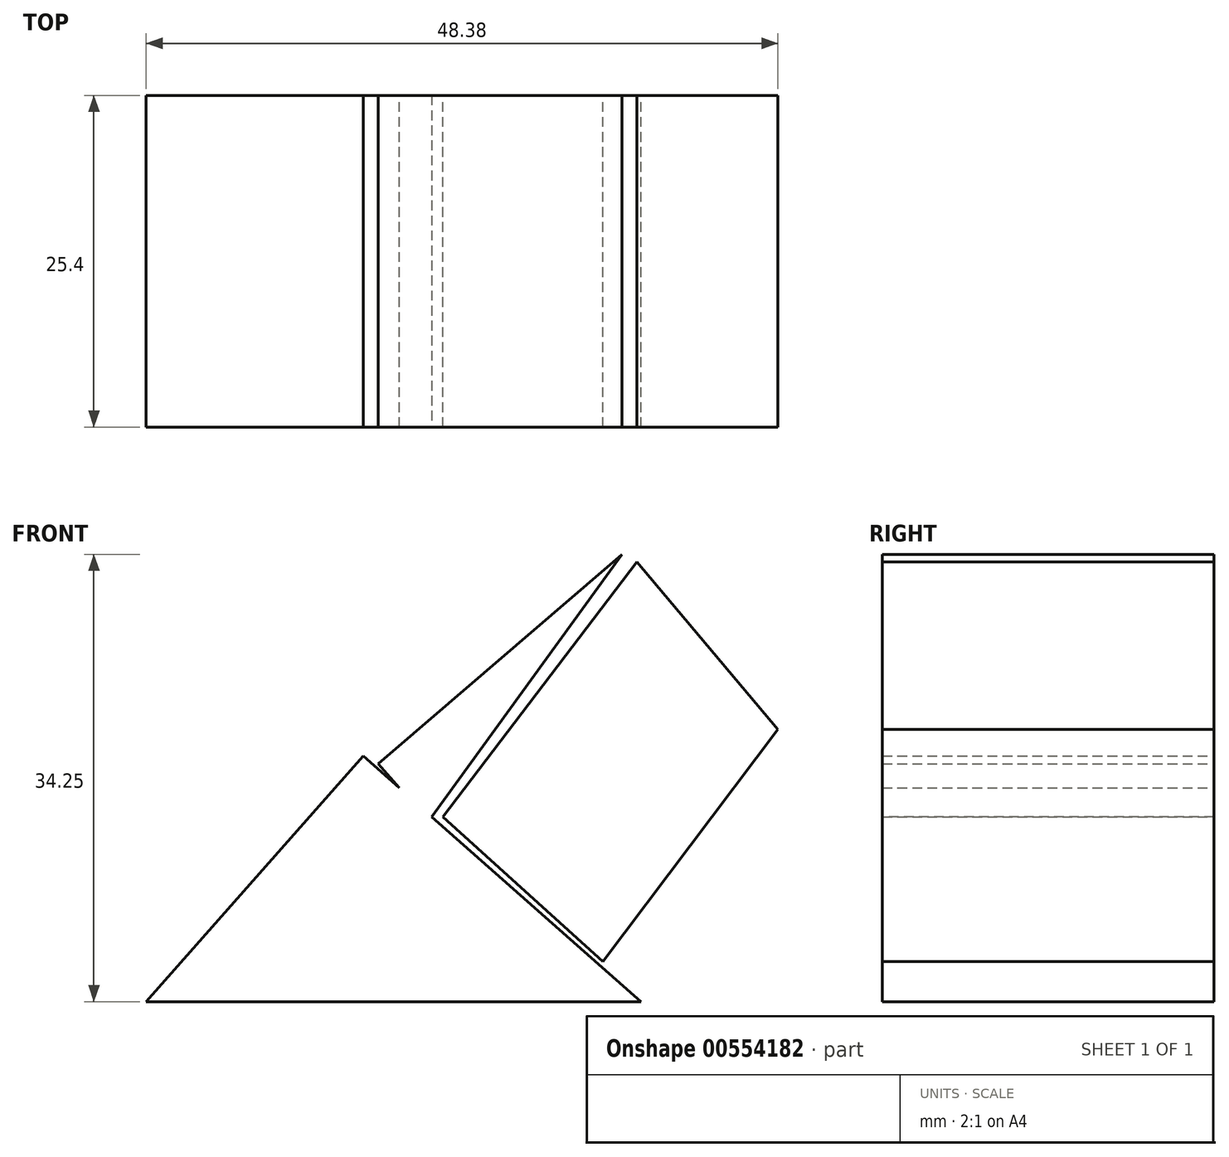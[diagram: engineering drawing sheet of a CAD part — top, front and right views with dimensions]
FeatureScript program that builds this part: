
annotation { "Feature Type Name" : "Feature", "Feature Type Description" : "" }
export const myFeature = defineFeature(function(context is Context, id is Id, definition is map)
    precondition{}
    {
        {
            var Q0;
            Q0=qCreatedBy(makeId("Front.planeOp"),FACE);
            var sketch = newSketch(context, id + "F0", { "sketchPlane" : qUnion([Q0])});
            skLineSegment(sketch, "E0", {"start": v(-48.38, 0) * mm, "end": v(-31.77, 18.8) * mm});
            skLineSegment(sketch, "E1", {"start": v(-31.77, 18.8) * mm, "end": v(-10.5, 0) * mm});
            skLineSegment(sketch, "E2", {"start": v(-10.5, 0) * mm, "end": v(-48.38, 0) * mm});
            skSolve(sketch);
        }
        {
            var Q0;
            Q0 = qSketchRegion(id + "F0", true);
            extrude(context, id + "F1", {"entities" : qUnion([Q0]), "depth" : 25.4 * mm, "offsetDistance" : 25.4 * mm});
        }
        {
            var Q0;
            Q0=qCreatedBy(makeId("Front.planeOp"),FACE);
            var sketch = newSketch(context, id + "F2", { "sketchPlane" : qUnion([Q0])});
            skLineSegment(sketch, "E3", {"start": v(-25.65, 14.14) * mm, "end": v(-10.78, 33.67) * mm});
            skLineSegment(sketch, "E4", {"start": v(-10.78, 33.67) * mm, "end": v(0, 20.84) * mm});
            skLineSegment(sketch, "E5", {"start": v(0, 20.84) * mm, "end": v(-13.4, 3.06) * mm});
            skLineSegment(sketch, "E6", {"start": v(-13.4, 3.06) * mm, "end": v(-25.65, 14.14) * mm});
            skSolve(sketch);
        }
        {
            var Q0;
            Q0 = qSketchRegion(id + "F2", true);
            extrude(context, id + "F3", {"entities" : qUnion([Q0]), "depth" : 25.4 * mm, "offsetDistance" : 25.4 * mm});
        }
        {
            var Q0;
            Q0=qCreatedBy(makeId("Front.planeOp"),FACE);
            var sketch = newSketch(context, id + "F4", { "sketchPlane" : qUnion([Q0])});
            skLineSegment(sketch, "E7", {"start": v(-11.95, 34.25) * mm, "end": v(-30.6, 18.22) * mm});
            skLineSegment(sketch, "E8", {"start": v(-30.6, 18.22) * mm, "end": v(-26.8, 13.78) * mm});
            skLineSegment(sketch, "E9", {"start": v(-26.8, 13.78) * mm, "end": v(-11.95, 34.25) * mm});
            skSolve(sketch);
        }
        {
            var Q0;
            Q0 = qSketchRegion(id + "F4", true);
            extrude(context, id + "F5", {"entities" : qUnion([Q0]), "operationType" : NewBodyOperationType.ADD, "depth" : 25.4 * mm, "offsetDistance" : 25.4 * mm});
        }
    });
